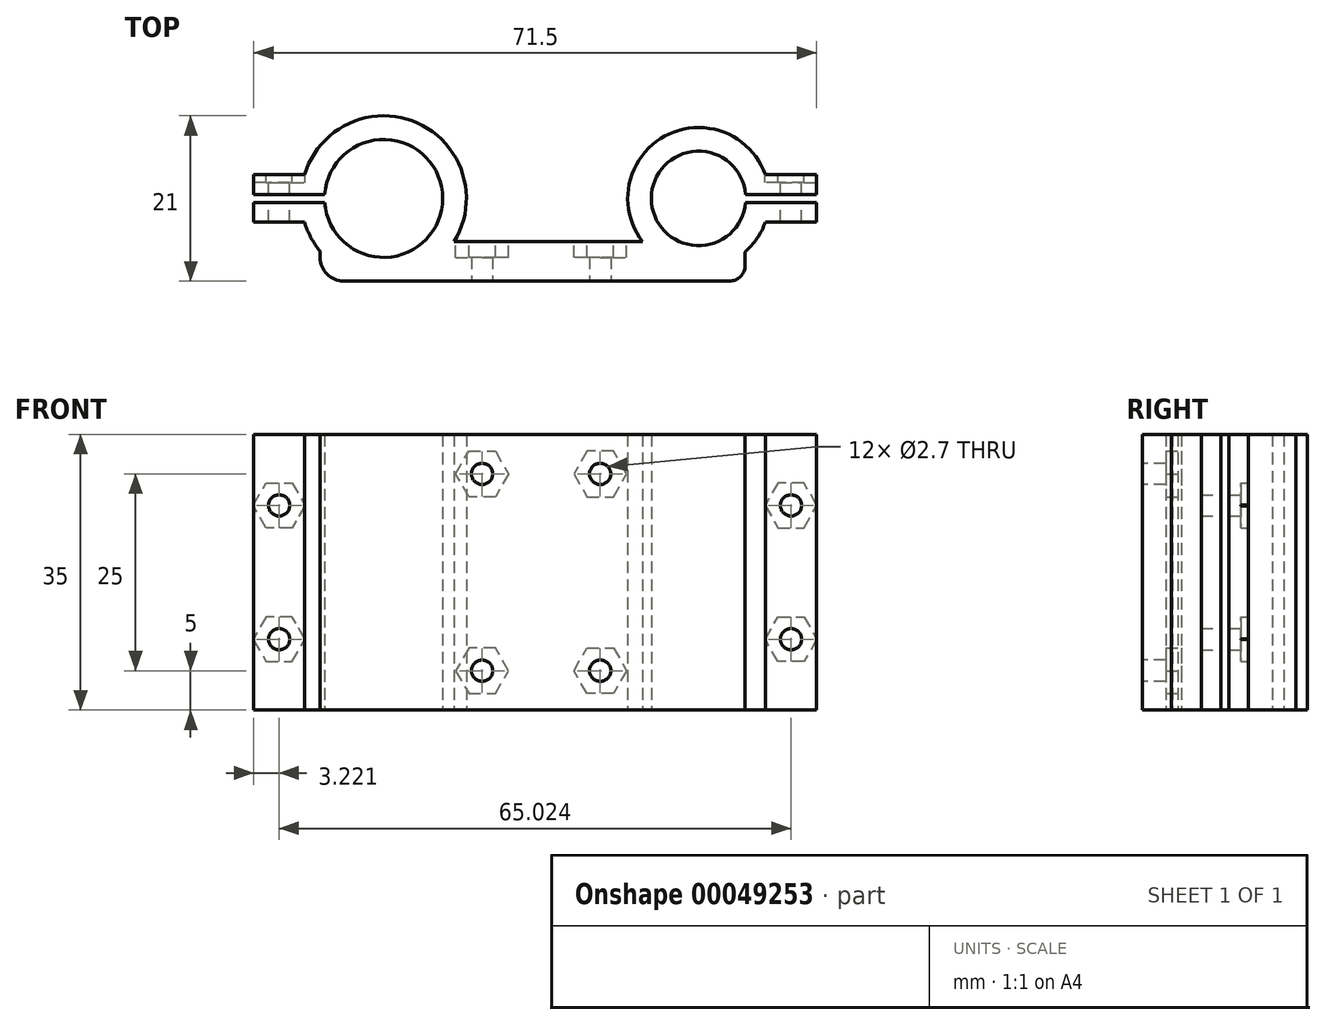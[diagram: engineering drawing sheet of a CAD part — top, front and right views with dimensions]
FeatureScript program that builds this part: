
annotation { "Feature Type Name" : "Feature", "Feature Type Description" : "" }
export const myFeature = defineFeature(function(context is Context, id is Id, definition is map)
    precondition{}
    {
        {
            var Q0;
            Q0=qCreatedBy(makeId("Top.planeOp"),FACE);
            var sketch = newSketch(context, id + "F0", { "sketchPlane" : qUnion([Q0])});
            skArc(sketch, "E0", {"start": v(-27.82, -25.7) * mm, "mid": v(-41.2, -21.15) * mm, "end": v(-42.53, -35.2) * mm});
            skArc(sketch, "E1", {"start": v(-30.33, -28.2) * mm, "mid": v(-42.3, -28.7) * mm, "end": v(-30.33, -29.2) * mm});
            skArc(sketch, "E2", {"start": v(-83.8, -29.2) * mm, "mid": v(-68.8, -28.7) * mm, "end": v(-83.8, -28.2) * mm});
            skArc(sketch, "E3", {"start": v(-86.37, -31.7) * mm, "mid": v(-85.57, -33.66) * mm, "end": v(-84.4, -35.4) * mm});
            skLineSegment(sketch, "E4", {"start": v(-42.53, -35.2) * mm, "end": v(-68.06, -35.2) * mm});
            skLineSegment(sketch, "E5", {"start": v(-84.4, -35.4) * mm, "end": v(-84.4, -36.2) * mm});
            skLineSegment(sketch, "E6", {"start": v(-81.4, -39.2) * mm, "end": v(-32.4, -39.2) * mm});
            skLineSegment(sketch, "E7", {"start": v(-30.4, -37.2) * mm, "end": v(-30.4, -35.5) * mm});
            skLineSegment(sketch, "E8", {"start": v(-76.3, -28.7) * mm, "end": v(-66.3, -28.7) * mm, "construction": true});
            skPoint(sketch, "E9", {"position": v(-56.3, -28.7) * mm});
            skLineSegment(sketch, "E10", {"start": v(-56.3, -28.7) * mm, "end": v(-51.3, -28.7) * mm, "construction": true});
            skLineSegment(sketch, "E11", {"start": v(-46.3, -28.7) * mm, "end": v(-36.3, -28.7) * mm, "construction": true});
            skLineSegment(sketch, "E12", {"start": v(-66.3, -28.7) * mm, "end": v(-61.3, -28.7) * mm, "construction": true});
            skLineSegment(sketch, "E13", {"start": v(-51.3, -28.7) * mm, "end": v(-46.3, -28.7) * mm, "construction": true});
            skLineSegment(sketch, "E14", {"start": v(-61.3, -28.7) * mm, "end": v(-56.3, -28.7) * mm, "construction": true});
            skPoint(sketch, "E15", {"position": v(-63.8, -28.7) * mm});
            skPoint(sketch, "E16", {"position": v(-48.8, -28.7) * mm});
            skPoint(sketch, "E17.visualSharp", {"position": v(-30.4, -39.2) * mm});
            skArc(sketch, "E17.filletArc", {"start": v(-32.4, -39.2) * mm, "mid": v(-30.98, -38.62) * mm, "end": v(-30.4, -37.2) * mm});
            skPoint(sketch, "E18", {"position": v(-76.3, -39.2) * mm});
            skLineSegment(sketch, "E19.rect.bottom", {"start": v(-92.8, -25.7) * mm, "end": v(-86.37, -25.7) * mm});
            skLineSegment(sketch, "E19.rect.top", {"start": v(-92.8, -31.7) * mm, "end": v(-86.37, -31.7) * mm});
            skLineSegment(sketch, "E19.rect.left", {"start": v(-92.8, -25.7) * mm, "end": v(-92.8, -28.2) * mm});
            skLineSegment(sketch, "E20.rect.right", {"start": v(-21.3, -25.7) * mm, "end": v(-21.3, -28.2) * mm});
            skLineSegment(sketch, "E21.rect.bottom", {"start": v(-92.8, -28.2) * mm, "end": v(-83.8, -28.2) * mm});
            skLineSegment(sketch, "E21.rect.top", {"start": v(-92.8, -29.2) * mm, "end": v(-83.8, -29.2) * mm});
            skPoint(sketch, "E22", {"position": v(-86.8, -29.2) * mm});
            skPoint(sketch, "E23", {"position": v(-86.8, -28.2) * mm});
            skPoint(sketch, "E24", {"position": v(-92.8, -28.2) * mm});
            skPoint(sketch, "E25", {"position": v(-92.8, -29.2) * mm});
            skPoint(sketch, "E26", {"position": v(-86.37, -25.7) * mm});
            skPoint(sketch, "E27", {"position": v(-86.37, -31.7) * mm});
            skPoint(sketch, "E28", {"position": v(-21.3, -28.2) * mm});
            skPoint(sketch, "E28.positionSnap0", {"position": v(-21.3, -28.7) * mm});
            skPoint(sketch, "E29", {"position": v(-21.3, -29.2) * mm});
            skPoint(sketch, "E30", {"position": v(-27.32, -28.2) * mm});
            skPoint(sketch, "E31", {"position": v(-27.32, -29.2) * mm});
            skPoint(sketch, "E32", {"position": v(-27.82, -31.7) * mm});
            skPoint(sketch, "E33", {"position": v(-31.11, -31.7) * mm});
            skPoint(sketch, "E34", {"position": v(-30.33, -28.2) * mm});
            skPoint(sketch, "E35", {"position": v(-27.82, -25.7) * mm});
            skPoint(sketch, "E21.rect.left.end.orphan", {"position": v(-94.34, -29.2) * mm});
            skPoint(sketch, "E21.rect.left.start.orphan", {"position": v(-94.34, -28.2) * mm});
            skLineSegment(sketch, "E36.trimOffspring", {"start": v(-92.8, -29.2) * mm, "end": v(-92.8, -31.7) * mm});
            skArc(sketch, "E37.trimOffspring", {"start": v(-68.06, -35.2) * mm, "mid": v(-71.47, -19.39) * mm, "end": v(-86.37, -25.7) * mm});
            skLineSegment(sketch, "E38.trimOffspring", {"start": v(-27.82, -31.7) * mm, "end": v(-21.3, -31.7) * mm});
            skLineSegment(sketch, "E39.trimOffspring", {"start": v(-30.33, -28.2) * mm, "end": v(-21.3, -28.2) * mm});
            skLineSegment(sketch, "E40.trimOffspring", {"start": v(-27.82, -25.7) * mm, "end": v(-21.3, -25.7) * mm});
            skPoint(sketch, "E41.orphan", {"position": v(-18.28, -28.2) * mm});
            skPoint(sketch, "E42.orphan", {"position": v(-18.28, -29.2) * mm});
            skLineSegment(sketch, "E43.trimOffspring", {"start": v(-21.3, -29.2) * mm, "end": v(-21.3, -31.7) * mm});
            skLineSegment(sketch, "E44.trimOffspring", {"start": v(-30.33, -29.2) * mm, "end": v(-21.3, -29.2) * mm});
            skPoint(sketch, "E45.visualSharp", {"position": v(-84.4, -39.2) * mm});
            skArc(sketch, "E45.filletArc", {"start": v(-84.4, -36.2) * mm, "mid": v(-83.51, -38.33) * mm, "end": v(-81.4, -39.2) * mm});
            skArc(sketch, "E46.trimOffspring", {"start": v(-30.4, -35.5) * mm, "mid": v(-28.87, -33.77) * mm, "end": v(-27.82, -31.7) * mm});
            skLineSegment(sketch, "E47", {"start": v(-56.3, -28.7) * mm, "end": v(-56.3, -39.2) * mm, "construction": true});
            skSolve(sketch);
        }
        {
            var Q0;
            Q0=makeQuery(id+"F0.imprint","IMPRINT",FACE,{"disambiguationData":[TD([[makeQuery(id+"F0.imprint","IMPRINT",EDGE,{"derivedFrom":sQuery(id+"F0.wireOp",EDGE,"E0")}),1.0]])]});
            var Q1;
            Q1=qSketchRegion(id+"F2",true);
            extrude(context, id + "F1", {"entities" : qUnion([Q0, Q1]), "depth" : 35 * mm});
        }
        {
            var Q0;
            Q0=makeQuery(id+"F1.opExtrude","SWEPT_FACE",FACE,{"disambiguationData":[OSD([sQuery(id+"F0.wireOp",EDGE,"E6")])]});
            var sketch = newSketch(context, id + "F2", { "sketchPlane" : qUnion([Q0])});
            skLineSegment(sketch, "E48", {"start": v(-56.3, 35) * mm, "end": v(-56.3, 17.5) * mm, "construction": true});
            skLineSegment(sketch, "E49", {"start": v(-56.3, 17.5) * mm, "end": v(-81.4, 17.5) * mm, "construction": true});
            skLineSegment(sketch, "E50", {"start": v(-56.3, 17.5) * mm, "end": v(-32.4, 17.5) * mm, "construction": true});
            skPoint(sketch, "E51", {"position": v(139.68, 0) * mm});
            skPoint(sketch, "E52", {"position": v(-60.88, -141.08) * mm});
            skPoint(sketch, "E53.end.orphan", {"position": v(-63.8, 35) * mm});
            skLineSegment(sketch, "E54", {"start": v(-63.8, 30) * mm, "end": v(-63.8, 35) * mm});
            skPoint(sketch, "E55", {"position": v(-63.8, 30) * mm});
            skLineSegment(sketch, "E56.MirrorCS", {"start": v(-48.8, 30) * mm, "end": v(-48.8, 35) * mm});
            skLineSegment(sketch, "E57.MirrorCS", {"start": v(-56.3, 17.5) * mm, "end": v(-80.22, 17.5) * mm, "construction": true});
            skLineSegment(sketch, "E58.MirrorCS", {"start": v(-48.8, 5) * mm, "end": v(-48.8, 0) * mm});
            skLineSegment(sketch, "E59.MirrorCS", {"start": v(-63.8, 5) * mm, "end": v(-63.8, 0) * mm});
            skPoint(sketch, "E60", {"position": v(-48.8, 30) * mm});
            skPoint(sketch, "E61", {"position": v(-48.8, 5) * mm});
            skPoint(sketch, "E62", {"position": v(-63.8, 5) * mm});
            skCircle(sketch, "E63.cCircle", {"center": v(-48.8, 30) * mm, "radius": 2.85 * mm, "construction": true});
            skLineSegment(sketch, "E63.0", {"start": v(-45.96, 31.65) * mm, "end": v(-45.96, 28.35) * mm});
            skLineSegment(sketch, "E63.1", {"start": v(-45.96, 28.35) * mm, "end": v(-48.8, 26.7) * mm});
            skLineSegment(sketch, "E63.2", {"start": v(-48.8, 26.7) * mm, "end": v(-51.66, 28.35) * mm});
            skLineSegment(sketch, "E63.3", {"start": v(-51.66, 28.35) * mm, "end": v(-51.66, 31.65) * mm});
            skLineSegment(sketch, "E63.4", {"start": v(-51.66, 31.65) * mm, "end": v(-48.8, 33.3) * mm});
            skLineSegment(sketch, "E63.5", {"start": v(-48.8, 33.3) * mm, "end": v(-45.96, 31.65) * mm});
            skPoint(sketch, "E63.0.midPoint", {"position": v(-45.96, 30) * mm});
            skLineSegment(sketch, "E64.MirrorCS", {"start": v(-35.6, 17.5) * mm, "end": v(-59.52, 17.5) * mm, "construction": true});
            skCircle(sketch, "E65.MirrorC", {"center": v(-48.8, 5) * mm, "radius": 2.85 * mm, "construction": true});
            skLineSegment(sketch, "E66.MirrorCS", {"start": v(-45.96, 3.35) * mm, "end": v(-45.96, 6.65) * mm});
            skLineSegment(sketch, "E67.MirrorCS", {"start": v(-48.8, 1.7) * mm, "end": v(-45.96, 3.35) * mm});
            skLineSegment(sketch, "E68.MirrorCS", {"start": v(-48.8, 8.3) * mm, "end": v(-51.66, 6.65) * mm});
            skPoint(sketch, "E69.MirrorP", {"position": v(-45.96, 5) * mm});
            skLineSegment(sketch, "E70.MirrorCS", {"start": v(-51.66, 3.35) * mm, "end": v(-48.8, 1.7) * mm});
            skLineSegment(sketch, "E71.MirrorCS", {"start": v(-51.66, 6.65) * mm, "end": v(-51.66, 3.35) * mm});
            skLineSegment(sketch, "E72.MirrorCS", {"start": v(-45.96, 6.65) * mm, "end": v(-48.8, 8.3) * mm});
            skLineSegment(sketch, "E73.MirrorCS", {"start": v(-66.66, 31.65) * mm, "end": v(-66.66, 28.35) * mm});
            skPoint(sketch, "E74.MirrorP", {"position": v(-66.66, 30) * mm});
            skCircle(sketch, "E75.MirrorC", {"center": v(-63.8, 30) * mm, "radius": 2.85 * mm, "construction": true});
            skLineSegment(sketch, "E76.MirrorCS", {"start": v(-66.66, 28.35) * mm, "end": v(-63.8, 26.7) * mm});
            skLineSegment(sketch, "E77.MirrorCS", {"start": v(-63.8, 26.7) * mm, "end": v(-60.96, 28.35) * mm});
            skLineSegment(sketch, "E78.MirrorCS", {"start": v(-60.96, 28.35) * mm, "end": v(-60.96, 31.65) * mm});
            skLineSegment(sketch, "E79.MirrorCS", {"start": v(-60.96, 31.65) * mm, "end": v(-63.8, 33.3) * mm});
            skLineSegment(sketch, "E80.MirrorCS", {"start": v(-63.8, 33.3) * mm, "end": v(-66.66, 31.65) * mm});
            skLineSegment(sketch, "E81.MirrorCS", {"start": v(-66.66, 3.35) * mm, "end": v(-66.66, 6.65) * mm});
            skPoint(sketch, "E82.MirrorP", {"position": v(-66.66, 5) * mm});
            skLineSegment(sketch, "E83.MirrorCS", {"start": v(-63.8, 8.3) * mm, "end": v(-60.96, 6.65) * mm});
            skLineSegment(sketch, "E84.MirrorCS", {"start": v(-60.96, 6.65) * mm, "end": v(-60.96, 3.35) * mm});
            skCircle(sketch, "E85.MirrorC", {"center": v(-63.8, 5) * mm, "radius": 2.85 * mm, "construction": true});
            skLineSegment(sketch, "E86.MirrorCS", {"start": v(-60.96, 3.35) * mm, "end": v(-63.8, 1.7) * mm});
            skLineSegment(sketch, "E87.MirrorCS", {"start": v(-66.66, 6.65) * mm, "end": v(-63.8, 8.3) * mm});
            skLineSegment(sketch, "E88.MirrorCS", {"start": v(-63.8, 1.7) * mm, "end": v(-66.66, 3.35) * mm});
            skCircle(sketch, "E89.MirrorC", {"center": v(-64.88, 27.43) * mm, "radius": 2.85 * mm, "construction": true});
            skArc(sketch, "E90", {"start": v(-38.46, 10.08) * mm, "mid": v(-51.83, 14.65) * mm, "end": v(-53.17, 0.58) * mm});
            skArc(sketch, "E91", {"start": v(-40.97, 7.58) * mm, "mid": v(-52.95, 7.08) * mm, "end": v(-40.97, 6.58) * mm});
            skArc(sketch, "E92", {"start": v(-94.43, 6.58) * mm, "mid": v(-79.45, 7.08) * mm, "end": v(-94.43, 7.58) * mm});
            skArc(sketch, "E93", {"start": v(-97, 4.08) * mm, "mid": v(-96.2, 2.14) * mm, "end": v(-95.03, 0.39) * mm});
            skLineSegment(sketch, "E94", {"start": v(-53.17, 0.58) * mm, "end": v(-78.7, 0.58) * mm});
            skLineSegment(sketch, "E95", {"start": v(-95.03, 0.39) * mm, "end": v(-95.03, -0.42) * mm});
            skLineSegment(sketch, "E96", {"start": v(-92.03, -3.42) * mm, "end": v(-43.04, -3.42) * mm});
            skLineSegment(sketch, "E97", {"start": v(-41.04, -1.42) * mm, "end": v(-41.04, 0.3) * mm});
            skLineSegment(sketch, "E98", {"start": v(-86.95, 7.08) * mm, "end": v(-76.95, 7.08) * mm, "construction": true});
            skPoint(sketch, "E99", {"position": v(-66.95, 7.08) * mm});
            skLineSegment(sketch, "E100", {"start": v(-66.95, 7.08) * mm, "end": v(-61.95, 7.08) * mm, "construction": true});
            skLineSegment(sketch, "E101", {"start": v(-56.95, 7.08) * mm, "end": v(-46.95, 7.08) * mm, "construction": true});
            skLineSegment(sketch, "E102", {"start": v(-76.95, 7.08) * mm, "end": v(-71.95, 7.08) * mm, "construction": true});
            skLineSegment(sketch, "E103", {"start": v(-61.95, 7.08) * mm, "end": v(-56.95, 7.08) * mm, "construction": true});
            skLineSegment(sketch, "E104", {"start": v(-71.95, 7.08) * mm, "end": v(-66.95, 7.08) * mm, "construction": true});
            skPoint(sketch, "E105", {"position": v(-74.45, 7.08) * mm});
            skPoint(sketch, "E106", {"position": v(-59.45, 7.08) * mm});
            skPoint(sketch, "E107.visualSharp", {"position": v(-41.04, -3.42) * mm});
            skArc(sketch, "E107.filletArc", {"start": v(-43.04, -3.42) * mm, "mid": v(-41.62, -2.83) * mm, "end": v(-41.04, -1.42) * mm});
            skPoint(sketch, "E108", {"position": v(-86.95, -3.42) * mm});
            skLineSegment(sketch, "E109.rect.bottom", {"start": v(-103.45, 10.08) * mm, "end": v(-97, 10.08) * mm});
            skLineSegment(sketch, "E109.rect.top", {"start": v(-103.45, 4.08) * mm, "end": v(-97, 4.08) * mm});
            skLineSegment(sketch, "E109.rect.left", {"start": v(-103.45, 10.08) * mm, "end": v(-103.45, 7.58) * mm});
            skLineSegment(sketch, "E110.rect.right", {"start": v(-31.95, 10.08) * mm, "end": v(-31.95, 7.58) * mm});
            skLineSegment(sketch, "E111.rect.bottom", {"start": v(-103.45, 7.58) * mm, "end": v(-94.43, 7.58) * mm});
            skLineSegment(sketch, "E111.rect.top", {"start": v(-103.45, 6.58) * mm, "end": v(-94.43, 6.58) * mm});
            skPoint(sketch, "E112", {"position": v(-97.43, 6.58) * mm});
            skPoint(sketch, "E113", {"position": v(-97.43, 7.58) * mm});
            skPoint(sketch, "E114", {"position": v(-103.45, 7.58) * mm});
            skPoint(sketch, "E115", {"position": v(-103.45, 6.58) * mm});
            skPoint(sketch, "E116", {"position": v(-97, 10.08) * mm});
            skPoint(sketch, "E117", {"position": v(-97, 4.08) * mm});
            skPoint(sketch, "E118", {"position": v(-31.95, 7.58) * mm});
            skPoint(sketch, "E118.positionSnap0", {"position": v(-31.95, 7.08) * mm});
            skPoint(sketch, "E119", {"position": v(-31.95, 6.58) * mm});
            skPoint(sketch, "E120", {"position": v(-37.96, 7.58) * mm});
            skPoint(sketch, "E121", {"position": v(-37.96, 6.58) * mm});
            skPoint(sketch, "E122", {"position": v(-38.46, 4.08) * mm});
            skPoint(sketch, "E123", {"position": v(-41.75, 4.08) * mm});
            skPoint(sketch, "E124", {"position": v(-40.97, 7.58) * mm});
            skPoint(sketch, "E125", {"position": v(-38.46, 10.08) * mm});
            skPoint(sketch, "E111.rect.left.end.orphan", {"position": v(-104.98, 6.58) * mm});
            skPoint(sketch, "E111.rect.left.start.orphan", {"position": v(-104.98, 7.58) * mm});
            skLineSegment(sketch, "E126.trimOffspring", {"start": v(-103.45, 6.58) * mm, "end": v(-103.45, 4.08) * mm});
            skArc(sketch, "E127.trimOffspring", {"start": v(-78.7, 0.58) * mm, "mid": v(-82.11, 16.4) * mm, "end": v(-97, 10.08) * mm});
            skLineSegment(sketch, "E128.trimOffspring", {"start": v(-38.46, 4.08) * mm, "end": v(-31.95, 4.08) * mm});
            skLineSegment(sketch, "E129.trimOffspring", {"start": v(-40.97, 7.58) * mm, "end": v(-31.95, 7.58) * mm});
            skLineSegment(sketch, "E130.trimOffspring", {"start": v(-38.46, 10.08) * mm, "end": v(-31.95, 10.08) * mm});
            skPoint(sketch, "E131.orphan", {"position": v(-28.91, 7.58) * mm});
            skPoint(sketch, "E132.orphan", {"position": v(-28.91, 6.58) * mm});
            skLineSegment(sketch, "E133.trimOffspring", {"start": v(-31.95, 6.58) * mm, "end": v(-31.95, 4.08) * mm});
            skLineSegment(sketch, "E134.trimOffspring", {"start": v(-40.97, 6.58) * mm, "end": v(-31.95, 6.58) * mm});
            skPoint(sketch, "E135.visualSharp", {"position": v(-95.03, -3.42) * mm});
            skArc(sketch, "E135.filletArc", {"start": v(-95.03, -0.42) * mm, "mid": v(-94.15, -2.54) * mm, "end": v(-92.03, -3.42) * mm});
            skArc(sketch, "E136.trimOffspring", {"start": v(-41.04, 0.3) * mm, "mid": v(-39.5, 2.02) * mm, "end": v(-38.46, 4.08) * mm});
            skLineSegment(sketch, "E137", {"start": v(-66.95, 7.08) * mm, "end": v(-66.95, -3.42) * mm, "construction": true});
            skSolve(sketch);
        }
        {
            var Q0;
            Q0=sQuery(id+"F2.wireOp",VERTEX,"E55");
            var Q1;
            Q1=sQuery(id+"F2.wireOp",VERTEX,"E60");
            var Q2;
            Q2=sQuery(id+"F2.wireOp",VERTEX,"E61");
            var Q3;
            Q3=sQuery(id+"F2.wireOp",VERTEX,"E62");
            var Q4;
            Q4=makeQuery(id+"F1.opExtrude","SWEPT_BODY",BODY,{"disambiguationData":[OSD([sQuery(id+"F0.wireOp",EDGE,"E0"),sQuery(id+"F0.wireOp",EDGE,"E1"),sQuery(id+"F0.wireOp",EDGE,"E2"),sQuery(id+"F0.wireOp",EDGE,"E3"),sQuery(id+"F0.wireOp",EDGE,"E4"),sQuery(id+"F0.wireOp",EDGE,"E5"),sQuery(id+"F0.wireOp",EDGE,"E6"),sQuery(id+"F0.wireOp",EDGE,"E7"),sQuery(id+"F0.wireOp",EDGE,"E17.filletArc"),sQuery(id+"F0.wireOp",EDGE,"E19.rect.bottom"),sQuery(id+"F0.wireOp",EDGE,"E19.rect.top"),sQuery(id+"F0.wireOp",EDGE,"E19.rect.left"),sQuery(id+"F0.wireOp",EDGE,"E20.rect.right"),sQuery(id+"F0.wireOp",EDGE,"E21.rect.bottom"),sQuery(id+"F0.wireOp",EDGE,"E21.rect.top"),sQuery(id+"F0.wireOp",EDGE,"E36.trimOffspring"),sQuery(id+"F0.wireOp",EDGE,"E37.trimOffspring"),sQuery(id+"F0.wireOp",EDGE,"E38.trimOffspring"),sQuery(id+"F0.wireOp",EDGE,"E39.trimOffspring"),sQuery(id+"F0.wireOp",EDGE,"E40.trimOffspring"),sQuery(id+"F0.wireOp",EDGE,"E43.trimOffspring"),sQuery(id+"F0.wireOp",EDGE,"E44.trimOffspring"),sQuery(id+"F0.wireOp",EDGE,"E45.filletArc"),sQuery(id+"F0.wireOp",EDGE,"E46.trimOffspring")])]});
            hole(context, id + "F3", {"style" : HoleStyle.SIMPLE, "holeDiameter" : 2.7 * mm, "endStyle" : HoleEndStyle.THROUGH, "locations" : qUnion([Q0, Q1, Q2, Q3]), "scope" : qUnion([Q4])});
        }
        {
            var Q0;
            Q0=makeQuery(id+"F1.opExtrude","SWEPT_FACE",FACE,{"disambiguationData":[OSD([sQuery(id+"F0.wireOp",EDGE,"E4")])]});
            var sketch = newSketch(context, id + "F4", { "sketchPlane" : qUnion([Q0])});
            skCircle(sketch, "E138.cCircle", {"center": v(48.8, 30) * mm, "radius": 2.9 * mm, "construction": true});
            skLineSegment(sketch, "E138.0", {"start": v(52.16, 30) * mm, "end": v(50.48, 27.1) * mm});
            skLineSegment(sketch, "E138.1", {"start": v(50.48, 27.1) * mm, "end": v(47.13, 27.1) * mm});
            skLineSegment(sketch, "E138.2", {"start": v(47.13, 27.1) * mm, "end": v(45.46, 30) * mm});
            skLineSegment(sketch, "E138.3", {"start": v(45.46, 30) * mm, "end": v(47.13, 32.9) * mm});
            skLineSegment(sketch, "E138.4", {"start": v(47.13, 32.9) * mm, "end": v(50.48, 32.9) * mm});
            skLineSegment(sketch, "E138.5", {"start": v(50.48, 32.9) * mm, "end": v(52.16, 30) * mm});
            skPoint(sketch, "E138.0.midPoint", {"position": v(51.32, 28.55) * mm});
            skPoint(sketch, "E139", {"position": v(55.3, 17.5) * mm});
            skLineSegment(sketch, "E140", {"start": v(55.3, 17.5) * mm, "end": v(65.53, 17.5) * mm});
            skCircle(sketch, "E141.MirrorC", {"center": v(48.8, 5) * mm, "radius": 2.9 * mm, "construction": true});
            skLineSegment(sketch, "E142.MirrorCS", {"start": v(50.48, 7.9) * mm, "end": v(47.13, 7.9) * mm});
            skLineSegment(sketch, "E143.MirrorCS", {"start": v(47.13, 2.1) * mm, "end": v(50.48, 2.1) * mm});
            skLineSegment(sketch, "E144.MirrorCS", {"start": v(45.46, 5) * mm, "end": v(47.13, 2.1) * mm});
            skLineSegment(sketch, "E145.MirrorCS", {"start": v(50.48, 2.1) * mm, "end": v(52.16, 5) * mm});
            skLineSegment(sketch, "E146.MirrorCS", {"start": v(52.16, 5) * mm, "end": v(50.48, 7.9) * mm});
            skPoint(sketch, "E147.MirrorP", {"position": v(51.32, 6.45) * mm});
            skLineSegment(sketch, "E148.MirrorCS", {"start": v(47.13, 7.9) * mm, "end": v(45.46, 5) * mm});
            skLineSegment(sketch, "E149", {"start": v(48.8, 30) * mm, "end": v(63.8, 30) * mm});
            skPoint(sketch, "E150", {"position": v(56.3, 30) * mm});
            skLineSegment(sketch, "E151", {"start": v(56.3, 30) * mm, "end": v(56.3, 17.5) * mm});
            skLineSegment(sketch, "E152.MirrorCS", {"start": v(67.16, 30) * mm, "end": v(65.48, 32.9) * mm});
            skCircle(sketch, "E153.MirrorC", {"center": v(63.8, 30) * mm, "radius": 2.9 * mm, "construction": true});
            skLineSegment(sketch, "E154.MirrorCS", {"start": v(62.13, 32.9) * mm, "end": v(60.46, 30) * mm});
            skLineSegment(sketch, "E155.MirrorCS", {"start": v(60.46, 30) * mm, "end": v(62.13, 27.1) * mm});
            skLineSegment(sketch, "E156.MirrorCS", {"start": v(63.8, 30) * mm, "end": v(48.8, 30) * mm});
            skLineSegment(sketch, "E157.MirrorCS", {"start": v(65.48, 32.9) * mm, "end": v(62.13, 32.9) * mm});
            skPoint(sketch, "E158.MirrorP", {"position": v(61.3, 28.55) * mm});
            skLineSegment(sketch, "E159.MirrorCS", {"start": v(62.13, 27.1) * mm, "end": v(65.48, 27.1) * mm});
            skLineSegment(sketch, "E160.MirrorCS", {"start": v(65.48, 27.1) * mm, "end": v(67.16, 30) * mm});
            skLineSegment(sketch, "E161.MirrorCS", {"start": v(65.48, 2.1) * mm, "end": v(62.13, 2.1) * mm});
            skLineSegment(sketch, "E162.MirrorCS", {"start": v(62.13, 7.9) * mm, "end": v(65.48, 7.9) * mm});
            skLineSegment(sketch, "E163.MirrorCS", {"start": v(62.13, 2.1) * mm, "end": v(60.46, 5) * mm});
            skCircle(sketch, "E164.MirrorC", {"center": v(63.8, 5) * mm, "radius": 2.9 * mm, "construction": true});
            skLineSegment(sketch, "E165.MirrorCS", {"start": v(67.16, 5) * mm, "end": v(65.48, 2.1) * mm});
            skLineSegment(sketch, "E166.MirrorCS", {"start": v(65.48, 7.9) * mm, "end": v(67.16, 5) * mm});
            skPoint(sketch, "E167.MirrorP", {"position": v(61.3, 6.45) * mm});
            skLineSegment(sketch, "E168.MirrorCS", {"start": v(60.46, 5) * mm, "end": v(62.13, 7.9) * mm});
            skSolve(sketch);
        }
        {
            var Q0;
            Q0=qSketchRegion(id+"F4",true);
            extrude(context, id + "F5", {"entities" : qUnion([Q0]), "operationType" : NewBodyOperationType.REMOVE, "oppositeDirection" : true, "depth" : 1 * mm});
        }
        {
            var Q0;
            Q0=makeQuery(id+"F1.opExtrude","SWEPT_FACE",FACE,{"disambiguationData":[OSD([sQuery(id+"F0.wireOp",EDGE,"E4")])]});
            extrude(context, id + "F6", {"entities" : qUnion([Q0]), "operationType" : NewBodyOperationType.ADD, "depth" : 1 * mm});
        }
        {
            var Q0;
            Q0=makeQuery(id+"F1.opExtrude","SWEPT_FACE",FACE,{"disambiguationData":[OSD([sQuery(id+"F0.wireOp",EDGE,"E19.rect.bottom")])]});
            var sketch = newSketch(context, id + "F7", { "sketchPlane" : qUnion([Q0])});
            skPoint(sketch, "E169", {"position": v(89.59, 35) * mm});
            skPoint(sketch, "E170", {"position": v(91.36, 17.5) * mm});
            skPoint(sketch, "E171", {"position": v(89.59, 17.5) * mm});
            skPoint(sketch, "E172", {"position": v(89.59, 26) * mm});
            skPoint(sketch, "E173", {"position": v(89.59, 9) * mm});
            skCircle(sketch, "E174.cCircle", {"center": v(89.59, 9) * mm, "radius": 2.85 * mm, "construction": true});
            skLineSegment(sketch, "E174.0", {"start": v(92.88, 9) * mm, "end": v(91.23, 6.15) * mm});
            skLineSegment(sketch, "E174.1", {"start": v(91.23, 6.15) * mm, "end": v(87.94, 6.15) * mm});
            skLineSegment(sketch, "E174.2", {"start": v(87.94, 6.15) * mm, "end": v(86.3, 9) * mm});
            skLineSegment(sketch, "E174.3", {"start": v(86.3, 9) * mm, "end": v(87.94, 11.85) * mm});
            skLineSegment(sketch, "E174.4", {"start": v(87.94, 11.85) * mm, "end": v(91.23, 11.85) * mm});
            skLineSegment(sketch, "E174.5", {"start": v(91.23, 11.85) * mm, "end": v(92.88, 9) * mm});
            skPoint(sketch, "E174.0.midPoint", {"position": v(92.06, 7.58) * mm});
            skLineSegment(sketch, "E175", {"start": v(91.36, 17.5) * mm, "end": v(89.59, 17.5) * mm, "construction": true});
            skLineSegment(sketch, "E176.MirrorCS", {"start": v(91.23, 28.85) * mm, "end": v(87.94, 28.85) * mm});
            skLineSegment(sketch, "E177.MirrorCS", {"start": v(92.88, 26) * mm, "end": v(91.23, 28.85) * mm});
            skCircle(sketch, "E178.MirrorC", {"center": v(89.59, 26) * mm, "radius": 2.85 * mm, "construction": true});
            skLineSegment(sketch, "E179.MirrorCS", {"start": v(87.94, 28.85) * mm, "end": v(86.3, 26) * mm});
            skLineSegment(sketch, "E180.MirrorCS", {"start": v(87.94, 23.15) * mm, "end": v(91.23, 23.15) * mm});
            skLineSegment(sketch, "E181.MirrorCS", {"start": v(86.3, 26) * mm, "end": v(87.94, 23.15) * mm});
            skLineSegment(sketch, "E182.MirrorCS", {"start": v(91.23, 23.15) * mm, "end": v(92.88, 26) * mm});
            skPoint(sketch, "E183.MirrorP", {"position": v(92.06, 27.42) * mm});
            skPoint(sketch, "E184.start.orphan", {"position": v(91.36, 26) * mm});
            skPoint(sketch, "E185.start.orphan", {"position": v(91.36, 9) * mm});
            skPoint(sketch, "E186.trimOffspring.end.orphan", {"position": v(89.59, 0) * mm});
            skSolve(sketch);
        }
        {
            var Q0;
            Q0=makeQuery(id+"F1.opExtrude","SWEPT_FACE",FACE,{"disambiguationData":[OSD([sQuery(id+"F0.wireOp",EDGE,"E40.trimOffspring")])]});
            var sketch = newSketch(context, id + "F8", { "sketchPlane" : qUnion([Q0])});
            skPoint(sketch, "E187", {"position": v(24.56, 35) * mm});
            skPoint(sketch, "E188", {"position": v(24.56, 0) * mm});
            skLineSegment(sketch, "E189", {"start": v(24.56, 35) * mm, "end": v(24.56, 0) * mm});
            skPoint(sketch, "E190", {"position": v(24.56, 17.5) * mm});
            skPoint(sketch, "E191", {"position": v(26.19, 17.5) * mm});
            skLineSegment(sketch, "E192", {"start": v(24.56, 17.5) * mm, "end": v(27.82, 17.5) * mm});
            skLineSegment(sketch, "E193", {"start": v(26.19, 11.85) * mm, "end": v(26.19, 9) * mm});
            skLineSegment(sketch, "E194.MirrorCS", {"start": v(26.19, 23.15) * mm, "end": v(26.19, 26) * mm});
            skLineSegment(sketch, "E195", {"start": v(26.19, 26) * mm, "end": v(22.2, 26) * mm});
            skLineSegment(sketch, "E196", {"start": v(26.19, 9) * mm, "end": v(22.28, 9) * mm});
            skPoint(sketch, "E197", {"position": v(24.56, 26) * mm});
            skPoint(sketch, "E198", {"position": v(24.56, 9) * mm});
            skCircle(sketch, "E199.cCircle", {"center": v(24.56, 26) * mm, "radius": 2.85 * mm, "construction": true});
            skLineSegment(sketch, "E199.0", {"start": v(27.86, 26) * mm, "end": v(26.21, 23.15) * mm});
            skLineSegment(sketch, "E199.1", {"start": v(26.21, 23.15) * mm, "end": v(22.92, 23.15) * mm});
            skLineSegment(sketch, "E199.2", {"start": v(22.92, 23.15) * mm, "end": v(21.27, 26) * mm});
            skLineSegment(sketch, "E199.3", {"start": v(21.27, 26) * mm, "end": v(22.92, 28.85) * mm});
            skLineSegment(sketch, "E199.4", {"start": v(22.92, 28.85) * mm, "end": v(26.21, 28.85) * mm});
            skLineSegment(sketch, "E199.5", {"start": v(26.21, 28.85) * mm, "end": v(27.86, 26) * mm});
            skPoint(sketch, "E199.0.midPoint", {"position": v(27.03, 24.57) * mm});
            skLineSegment(sketch, "E200.MirrorCS", {"start": v(27.86, 9) * mm, "end": v(26.21, 11.85) * mm});
            skLineSegment(sketch, "E201.MirrorCS", {"start": v(26.21, 11.85) * mm, "end": v(22.92, 11.85) * mm});
            skLineSegment(sketch, "E202.MirrorCS", {"start": v(26.21, 6.15) * mm, "end": v(27.86, 9) * mm});
            skLineSegment(sketch, "E203.MirrorCS", {"start": v(22.92, 11.85) * mm, "end": v(21.27, 9) * mm});
            skPoint(sketch, "E204.MirrorP", {"position": v(27.03, 10.43) * mm});
            skLineSegment(sketch, "E205.MirrorCS", {"start": v(26.19, 9) * mm, "end": v(22.2, 9) * mm});
            skLineSegment(sketch, "E206.MirrorCS", {"start": v(22.92, 6.15) * mm, "end": v(26.21, 6.15) * mm});
            skLineSegment(sketch, "E207.MirrorCS", {"start": v(21.27, 9) * mm, "end": v(22.92, 6.15) * mm});
            skSolve(sketch);
        }
        {
            var Q0;
            Q0=sQuery(id+"F8.wireOp",VERTEX,"E197");
            var Q1;
            Q1=sQuery(id+"F8.wireOp",VERTEX,"E198");
            var Q2;
            Q2=sQuery(id+"F7.wireOp",VERTEX,"E173");
            var Q3;
            Q3=sQuery(id+"F7.wireOp",VERTEX,"E172");
            var Q4;
            Q4=makeQuery(id+"F1.opExtrude","SWEPT_BODY",BODY,{"disambiguationData":[OSD([sQuery(id+"F0.wireOp",EDGE,"E0"),sQuery(id+"F0.wireOp",EDGE,"E1"),sQuery(id+"F0.wireOp",EDGE,"E2"),sQuery(id+"F0.wireOp",EDGE,"E3"),sQuery(id+"F0.wireOp",EDGE,"E4"),sQuery(id+"F0.wireOp",EDGE,"E5"),sQuery(id+"F0.wireOp",EDGE,"E6"),sQuery(id+"F0.wireOp",EDGE,"E7"),sQuery(id+"F0.wireOp",EDGE,"E17.filletArc"),sQuery(id+"F0.wireOp",EDGE,"E19.rect.bottom"),sQuery(id+"F0.wireOp",EDGE,"E19.rect.top"),sQuery(id+"F0.wireOp",EDGE,"E19.rect.left"),sQuery(id+"F0.wireOp",EDGE,"E20.rect.right"),sQuery(id+"F0.wireOp",EDGE,"E21.rect.bottom"),sQuery(id+"F0.wireOp",EDGE,"E21.rect.top"),sQuery(id+"F0.wireOp",EDGE,"E36.trimOffspring"),sQuery(id+"F0.wireOp",EDGE,"E37.trimOffspring"),sQuery(id+"F0.wireOp",EDGE,"E38.trimOffspring"),sQuery(id+"F0.wireOp",EDGE,"E39.trimOffspring"),sQuery(id+"F0.wireOp",EDGE,"E40.trimOffspring"),sQuery(id+"F0.wireOp",EDGE,"E43.trimOffspring"),sQuery(id+"F0.wireOp",EDGE,"E44.trimOffspring"),sQuery(id+"F0.wireOp",EDGE,"E45.filletArc"),sQuery(id+"F0.wireOp",EDGE,"E46.trimOffspring")])]});
            hole(context, id + "F9", {"style" : HoleStyle.SIMPLE, "holeDiameter" : 2.7 * mm, "endStyle" : HoleEndStyle.THROUGH, "locations" : qUnion([Q0, Q1, Q2, Q3]), "scope" : qUnion([Q4])});
        }
        {
            var Q0;
            Q0=qSketchRegion(id+"F8",true);
            extrude(context, id + "F10", {"entities" : qUnion([Q0]), "operationType" : NewBodyOperationType.REMOVE, "oppositeDirection" : true, "depth" : 1 * mm});
        }
        {
            var Q0;
            Q0=qSketchRegion(id+"F7",true);
            extrude(context, id + "F11", {"entities" : qUnion([Q0]), "operationType" : NewBodyOperationType.REMOVE, "oppositeDirection" : true, "depth" : 1 * mm});
        }
    });
